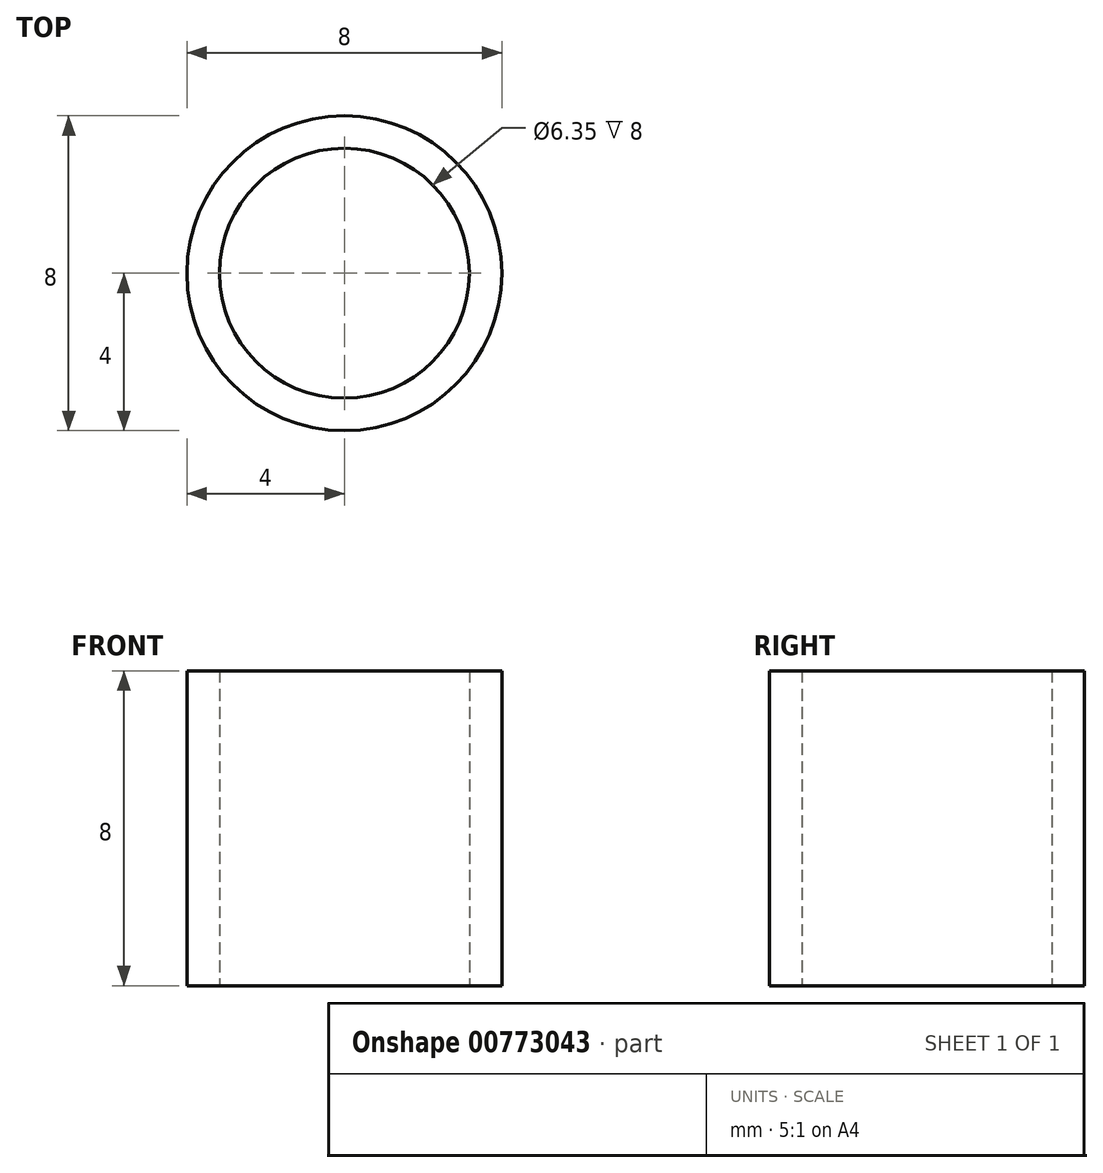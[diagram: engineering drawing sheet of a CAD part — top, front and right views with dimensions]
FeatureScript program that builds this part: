
annotation { "Feature Type Name" : "Feature", "Feature Type Description" : "" }
export const myFeature = defineFeature(function(context is Context, id is Id, definition is map)
    precondition{}
    {
        {
            var Q0;
            Q0=qCreatedBy(makeId("Top.planeOp"),FACE);
            var sketch = newSketch(context, id + "F0", { "sketchPlane" : qUnion([Q0])});
            skCircle(sketch, "E0", {"center": v(0, 0) * mm, "radius": 4 * mm});
            skCircle(sketch, "E1", {"center": v(0, 0) * mm, "radius": 3.18 * mm});
            skSolve(sketch);
        }
        {
            var Q0;
            Q0=makeQuery(id+"F0.imprint","IMPRINT",FACE,{"disambiguationData":[TD([[makeQuery(id+"F0.imprint","IMPRINT",EDGE,{"derivedFrom":sQuery(id+"F0.wireOp",EDGE,"E0")}),1.0]])]});
            extrude(context, id + "F1", {"entities" : qUnion([Q0]), "depth" : 8 * mm, "offsetDistance" : 25 * mm});
        }
    });
